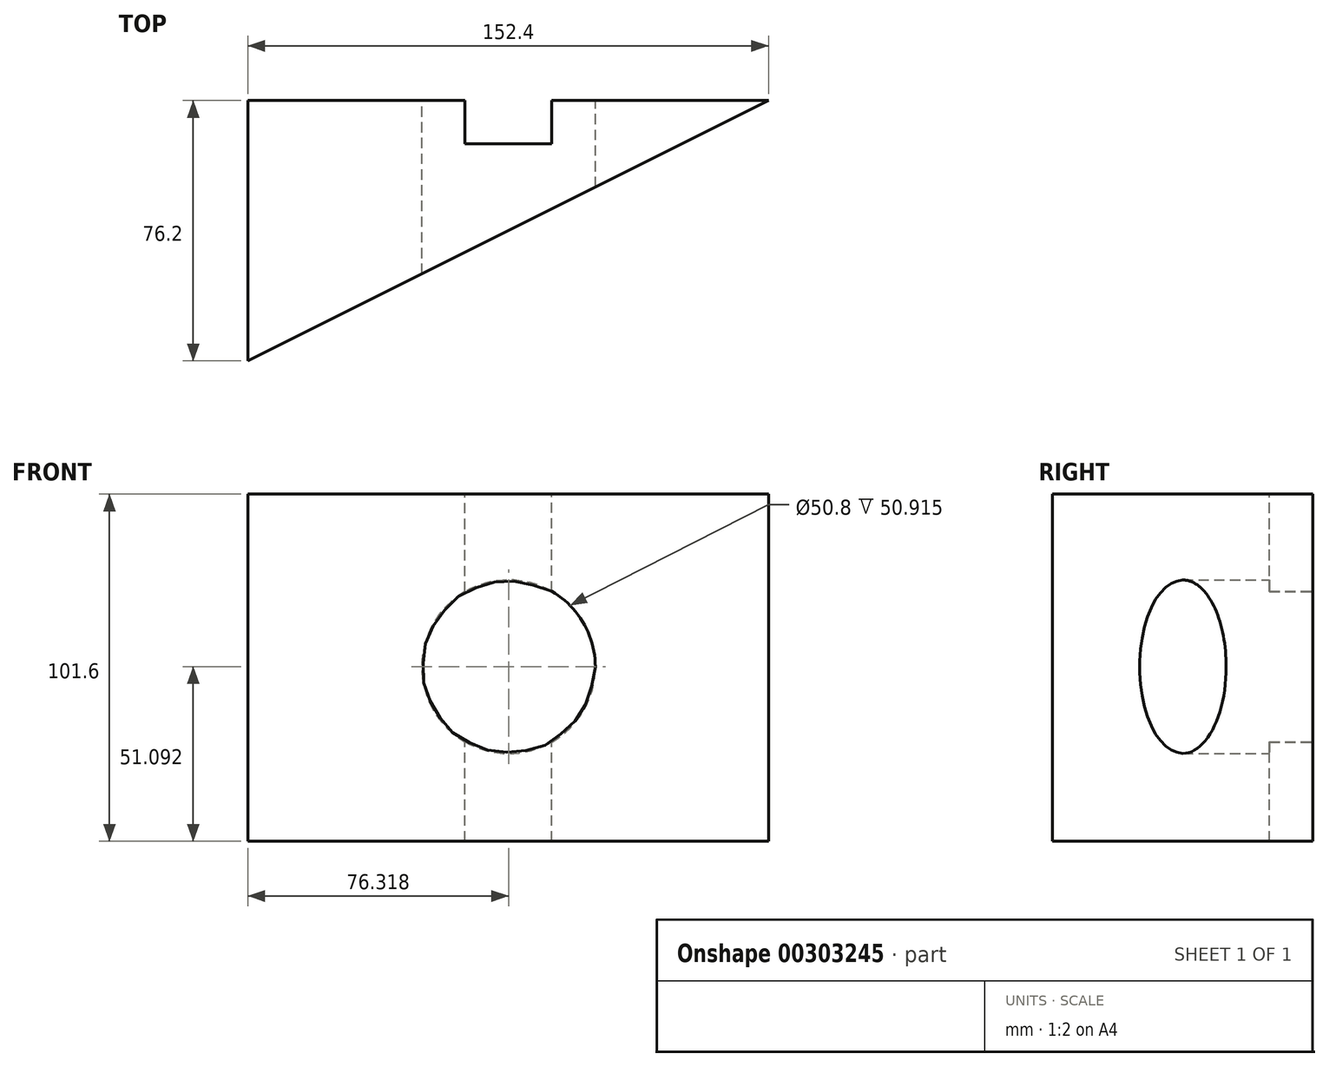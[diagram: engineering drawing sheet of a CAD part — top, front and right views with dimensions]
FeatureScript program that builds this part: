
annotation { "Feature Type Name" : "Feature", "Feature Type Description" : "" }
export const myFeature = defineFeature(function(context is Context, id is Id, definition is map)
    precondition{}
    {
        {
            var Q0;
            Q0=qCreatedBy(makeId("Top.planeOp"),FACE);
            var sketch = newSketch(context, id + "F0", { "sketchPlane" : qUnion([Q0])});
            skLineSegment(sketch, "E0.bottom", {"start": v(0, 0) * mm, "end": v(152.4, 0) * mm});
            skLineSegment(sketch, "E0.top", {"start": v(0, 76.2) * mm, "end": v(152.4, 76.2) * mm});
            skLineSegment(sketch, "E0.left", {"start": v(0, 0) * mm, "end": v(0, 76.2) * mm});
            skLineSegment(sketch, "E0.right", {"start": v(152.4, 0) * mm, "end": v(152.4, 76.2) * mm});
            skLineSegment(sketch, "E1", {"start": v(0, 0) * mm, "end": v(152.4, 76.2) * mm});
            skSolve(sketch);
        }
        {
            var Q0;
            Q0=makeQuery(id+"F0.imprint","IMPRINT",FACE,{"disambiguationData":[TD([[makeQuery(id+"F0.imprint","IMPRINT",EDGE,{"derivedFrom":sQuery(id+"F0.wireOp",EDGE,"E0.top")}),-1.0]])]});
            extrude(context, id + "F1", {"entities" : qUnion([Q0]), "oppositeDirection" : true, "depth" : 101.6 * mm});
        }
        {
            var Q0;
            Q0=makeQuery(id+"F1.opExtrude","SWEPT_FACE",FACE,{"disambiguationData":[OSD([sQuery(id+"F0.wireOp",EDGE,"E0.top")])]});
            var sketch = newSketch(context, id + "F2", { "sketchPlane" : qUnion([Q0])});
            skLineSegment(sketch, "E2.bottom", {"start": v(-88.9, -101.6) * mm, "end": v(-63.5, -101.6) * mm});
            skLineSegment(sketch, "E2.top", {"start": v(-88.9, 0) * mm, "end": v(-63.5, 0) * mm});
            skLineSegment(sketch, "E2.left", {"start": v(-88.9, -101.6) * mm, "end": v(-88.9, 0) * mm});
            skLineSegment(sketch, "E2.right", {"start": v(-63.5, -101.6) * mm, "end": v(-63.5, 0) * mm});
            skPoint(sketch, "E2.middle", {"position": v(-76.2, -50.8) * mm});
            skPoint(sketch, "E2.middle.positionSnap0", {"position": v(-76.2, -101.6) * mm});
            skPoint(sketch, "E2.centerSnap0", {"position": v(-76.2, -101.6) * mm});
            skSolve(sketch);
        }
        {
            var Q0;
            Q0=makeQuery(id+"F2.imprint","IMPRINT",FACE,{"disambiguationData":[TD([[makeQuery(id+"F2.imprint","IMPRINT",EDGE,{"derivedFrom":sQuery(id+"F2.wireOp",EDGE,"E2.bottom")}),-1.0]])]});
            extrude(context, id + "F3", {"entities" : qUnion([Q0]), "operationType" : NewBodyOperationType.REMOVE, "oppositeDirection" : true, "depth" : 12.7 * mm});
        }
        {
            var Q0;
            {var subQ0=sQuery(id+"F0.wireOp",EDGE,"E1");var subQ2=sQuery(id+"F0.wireOp",EDGE,"E0.top");Q0=makeQuery(id+"F3.boolean.opBoolean","SPLIT",FACE,{"disambiguationData":[TD([makeQuery(id+"F1.opExtrude","SWEPT_FACE",FACE,{"disambiguationData":[OSD([subQ0])]})])],"derivedFrom":makeQuery(id+"F1.opExtrude","SWEPT_FACE",FACE,{"disambiguationData":[OSD([subQ2])]})});}
            var sketch = newSketch(context, id + "F4", { "sketchPlane" : qUnion([Q0])});
            skCircle(sketch, "E3", {"center": v(-76.32, -50.5) * mm, "radius": 25.4 * mm});
            skSolve(sketch);
        }
        {
            var Q0;
            {var subQ0=sQuery(id+"F4.wireOp",EDGE,"E3");var subQ1=makeQuery(id+"F3.boolean.opBoolean","COPY",EDGE,{"derivedFrom":makeQuery(id+"F3.opExtrude","CAP_EDGE",EDGE,{"disambiguationData":[OSD([sQuery(id+"F2.wireOp",EDGE,"E2.left")])],"isStart":true})});var subQ2=makeQuery(id+"F4.imprint","INTERSECT",VERTEX,{"disambiguationData":[OD(0.0)],"derivedFrom":[subQ1,subQ0]});Q0=makeQuery(id+"F4.imprint","IMPRINT",FACE,{"disambiguationData":[TD([[makeQuery(id+"F4.imprint","IMPRINT",EDGE,{"disambiguationData":[TD([[subQ2,-1.0]])],"derivedFrom":subQ0}),1.0]])]});}
            var Q1;
            {var subQ0=sQuery(id+"F4.wireOp",EDGE,"E3");var subQ1=makeQuery(id+"F3.boolean.opBoolean","COPY",EDGE,{"derivedFrom":makeQuery(id+"F3.opExtrude","CAP_EDGE",EDGE,{"disambiguationData":[OSD([sQuery(id+"F2.wireOp",EDGE,"E2.left")])],"isStart":true})});var subQ2=makeQuery(id+"F4.imprint","INTERSECT",VERTEX,{"disambiguationData":[OD(0.0)],"derivedFrom":[subQ1,subQ0]});Q1=makeQuery(id+"F4.imprint","IMPRINT",FACE,{"disambiguationData":[TD([[makeQuery(id+"F4.imprint","IMPRINT",EDGE,{"disambiguationData":[TD([[subQ2,1.0]])],"derivedFrom":subQ0}),1.0]])]});}
            extrude(context, id + "F5", {"entities" : qUnion([Q0, Q1]), "operationType" : NewBodyOperationType.REMOVE, "endBound" : BoundingType.THROUGH_ALL, "oppositeDirection" : true, "depth" : 25.4 * mm});
        }
    });
